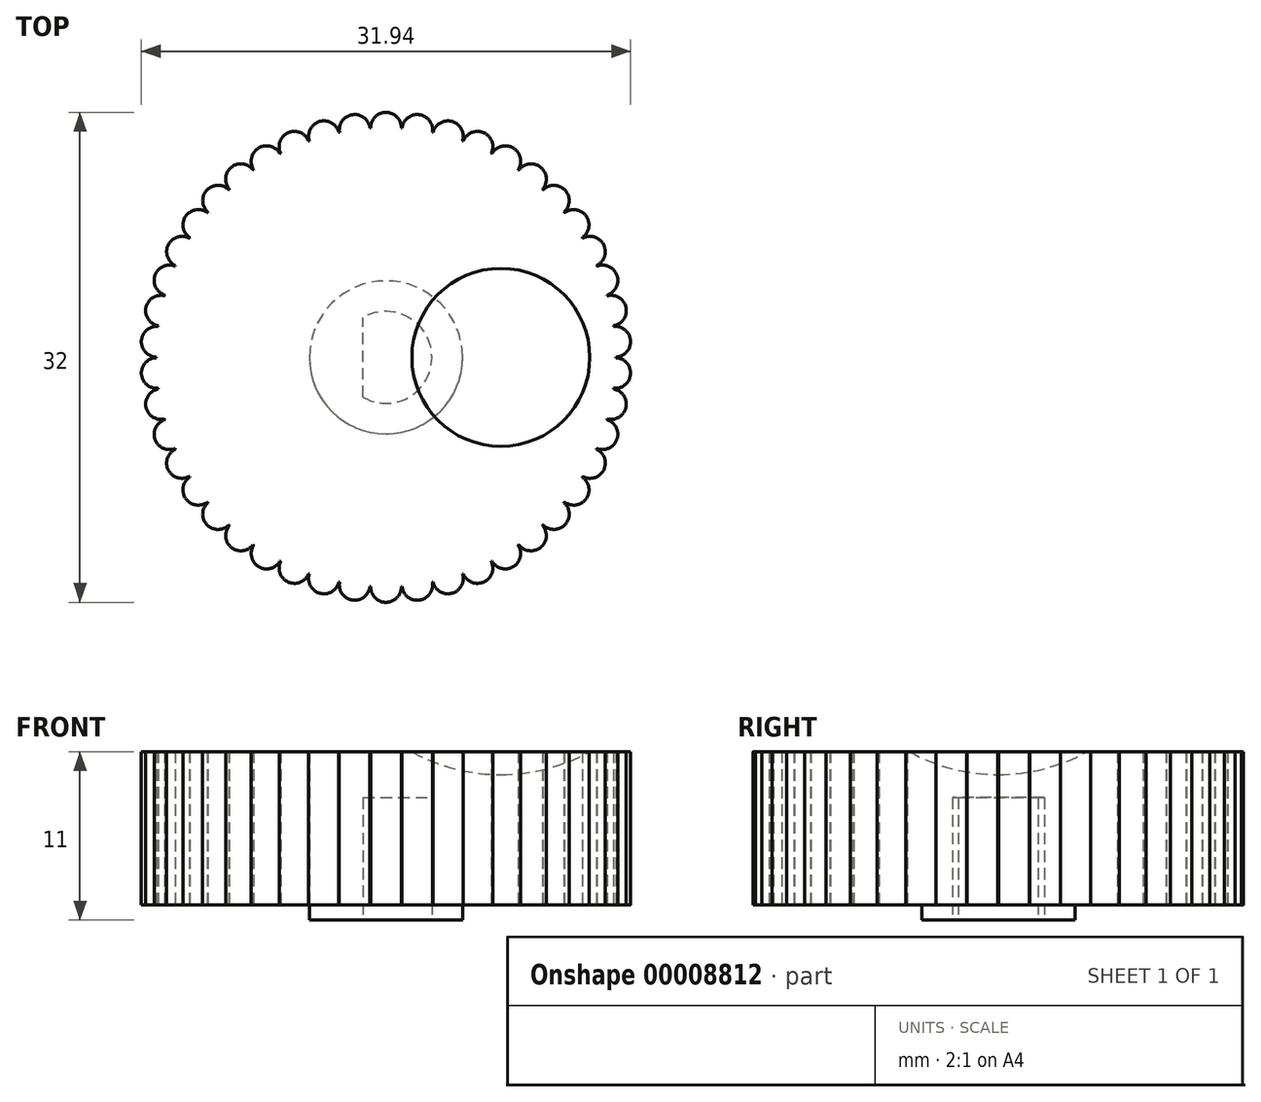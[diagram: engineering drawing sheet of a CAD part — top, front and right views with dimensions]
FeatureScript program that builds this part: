
annotation { "Feature Type Name" : "Feature", "Feature Type Description" : "" }
export const myFeature = defineFeature(function(context is Context, id is Id, definition is map)
    precondition{}
    {
        {
            var Q0;
            Q0=qCreatedBy(makeId("Top.planeOp"),FACE);
            var sketch = newSketch(context, id + "F0", { "sketchPlane" : qUnion([Q0])});
            skArc(sketch, "E0", {"start": v(1, 14.97) * mm, "mid": v(0, 16) * mm, "end": v(-1, 14.97) * mm});
            skCircle(sketch, "E1", {"center": v(0, 0) * mm, "radius": 15 * mm});
            skArc(sketch, "E2.1.0", {"start": v(-1.05, 14.96) * mm, "mid": v(-2.18, 15.85) * mm, "end": v(-3.03, 14.7) * mm});
            skArc(sketch, "E2.2.0", {"start": v(-3.08, 14.68) * mm, "mid": v(-4.32, 15.4) * mm, "end": v(-5, 14.14) * mm});
            skArc(sketch, "E2.3.0", {"start": v(-5.05, 14.13) * mm, "mid": v(-6.37, 14.68) * mm, "end": v(-6.88, 13.33) * mm});
            skArc(sketch, "E2.4.0", {"start": v(-6.92, 13.3) * mm, "mid": v(-8.31, 13.67) * mm, "end": v(-8.63, 12.27) * mm});
            skArc(sketch, "E2.5.0", {"start": v(-8.67, 12.24) * mm, "mid": v(-10.1, 12.41) * mm, "end": v(-10.22, 10.98) * mm});
            skArc(sketch, "E2.6.0", {"start": v(-10.26, 10.95) * mm, "mid": v(-11.7, 10.92) * mm, "end": v(-11.62, 9.49) * mm});
            skArc(sketch, "E2.7.0", {"start": v(-11.65, 9.45) * mm, "mid": v(-13.07, 9.23) * mm, "end": v(-12.8, 7.81) * mm});
            skArc(sketch, "E2.8.0", {"start": v(-12.83, 7.77) * mm, "mid": v(-14.2, 7.36) * mm, "end": v(-13.75, 6) * mm});
            skArc(sketch, "E2.9.0", {"start": v(-13.77, 5.95) * mm, "mid": v(-15.08, 5.36) * mm, "end": v(-14.44, 4.07) * mm});
            skArc(sketch, "E2.10.0", {"start": v(-14.45, 4.02) * mm, "mid": v(-15.67, 3.26) * mm, "end": v(-14.86, 2.07) * mm});
            skArc(sketch, "E2.11.0", {"start": v(-14.86, 2.02) * mm, "mid": v(-15.96, 1.1) * mm, "end": v(-15, 0.02) * mm});
            skArc(sketch, "E2.12.0", {"start": v(-15, -0.02) * mm, "mid": v(-15.96, -1.1) * mm, "end": v(-14.86, -2.02) * mm});
            skArc(sketch, "E2.13.0", {"start": v(-14.86, -2.07) * mm, "mid": v(-15.67, -3.26) * mm, "end": v(-14.45, -4.02) * mm});
            skArc(sketch, "E2.14.0", {"start": v(-14.44, -4.07) * mm, "mid": v(-15.08, -5.36) * mm, "end": v(-13.77, -5.95) * mm});
            skArc(sketch, "E2.15.0", {"start": v(-13.75, -6) * mm, "mid": v(-14.2, -7.36) * mm, "end": v(-12.83, -7.77) * mm});
            skArc(sketch, "E2.16.0", {"start": v(-12.8, -7.81) * mm, "mid": v(-13.07, -9.23) * mm, "end": v(-11.65, -9.45) * mm});
            skArc(sketch, "E2.17.0", {"start": v(-11.62, -9.49) * mm, "mid": v(-11.7, -10.92) * mm, "end": v(-10.26, -10.95) * mm});
            skArc(sketch, "E2.18.0", {"start": v(-10.22, -10.98) * mm, "mid": v(-10.1, -12.41) * mm, "end": v(-8.67, -12.24) * mm});
            skArc(sketch, "E2.19.0", {"start": v(-8.63, -12.27) * mm, "mid": v(-8.31, -13.67) * mm, "end": v(-6.92, -13.3) * mm});
            skArc(sketch, "E2.20.0", {"start": v(-6.88, -13.33) * mm, "mid": v(-6.37, -14.68) * mm, "end": v(-5.05, -14.13) * mm});
            skArc(sketch, "E2.21.0", {"start": v(-5, -14.14) * mm, "mid": v(-4.32, -15.4) * mm, "end": v(-3.08, -14.68) * mm});
            skArc(sketch, "E2.22.0", {"start": v(-3.03, -14.7) * mm, "mid": v(-2.18, -15.85) * mm, "end": v(-1.05, -14.96) * mm});
            skArc(sketch, "E2.23.0", {"start": v(-1, -14.97) * mm, "mid": v(0, -16) * mm, "end": v(1, -14.97) * mm});
            skArc(sketch, "E2.24.0", {"start": v(1.05, -14.96) * mm, "mid": v(2.18, -15.85) * mm, "end": v(3.03, -14.7) * mm});
            skArc(sketch, "E2.25.0", {"start": v(3.08, -14.68) * mm, "mid": v(4.32, -15.4) * mm, "end": v(5, -14.14) * mm});
            skArc(sketch, "E2.26.0", {"start": v(5.05, -14.13) * mm, "mid": v(6.37, -14.68) * mm, "end": v(6.88, -13.33) * mm});
            skArc(sketch, "E2.27.0", {"start": v(6.92, -13.3) * mm, "mid": v(8.31, -13.67) * mm, "end": v(8.63, -12.27) * mm});
            skArc(sketch, "E2.28.0", {"start": v(8.67, -12.24) * mm, "mid": v(10.1, -12.41) * mm, "end": v(10.22, -10.98) * mm});
            skArc(sketch, "E2.29.0", {"start": v(10.26, -10.95) * mm, "mid": v(11.7, -10.92) * mm, "end": v(11.62, -9.49) * mm});
            skArc(sketch, "E2.30.0", {"start": v(11.65, -9.45) * mm, "mid": v(13.07, -9.23) * mm, "end": v(12.8, -7.81) * mm});
            skArc(sketch, "E2.31.0", {"start": v(12.83, -7.77) * mm, "mid": v(14.2, -7.36) * mm, "end": v(13.75, -6) * mm});
            skArc(sketch, "E2.32.0", {"start": v(13.77, -5.95) * mm, "mid": v(15.08, -5.36) * mm, "end": v(14.44, -4.07) * mm});
            skArc(sketch, "E2.33.0", {"start": v(14.45, -4.02) * mm, "mid": v(15.67, -3.26) * mm, "end": v(14.86, -2.07) * mm});
            skArc(sketch, "E2.34.0", {"start": v(14.86, -2.02) * mm, "mid": v(15.96, -1.1) * mm, "end": v(15, -0.02) * mm});
            skArc(sketch, "E2.35.0", {"start": v(15, 0.02) * mm, "mid": v(15.96, 1.1) * mm, "end": v(14.86, 2.02) * mm});
            skArc(sketch, "E2.36.0", {"start": v(14.86, 2.07) * mm, "mid": v(15.67, 3.26) * mm, "end": v(14.45, 4.02) * mm});
            skArc(sketch, "E2.37.0", {"start": v(14.44, 4.07) * mm, "mid": v(15.08, 5.36) * mm, "end": v(13.77, 5.95) * mm});
            skArc(sketch, "E2.38.0", {"start": v(13.75, 6) * mm, "mid": v(14.2, 7.36) * mm, "end": v(12.83, 7.77) * mm});
            skArc(sketch, "E2.39.0", {"start": v(12.8, 7.81) * mm, "mid": v(13.07, 9.23) * mm, "end": v(11.65, 9.45) * mm});
            skArc(sketch, "E2.40.0", {"start": v(11.62, 9.49) * mm, "mid": v(11.7, 10.92) * mm, "end": v(10.26, 10.95) * mm});
            skArc(sketch, "E2.41.0", {"start": v(10.22, 10.98) * mm, "mid": v(10.1, 12.41) * mm, "end": v(8.67, 12.24) * mm});
            skArc(sketch, "E2.42.0", {"start": v(8.63, 12.27) * mm, "mid": v(8.31, 13.67) * mm, "end": v(6.92, 13.3) * mm});
            skArc(sketch, "E2.43.0", {"start": v(6.88, 13.33) * mm, "mid": v(6.37, 14.68) * mm, "end": v(5.05, 14.13) * mm});
            skArc(sketch, "E2.44.0", {"start": v(5, 14.14) * mm, "mid": v(4.32, 15.4) * mm, "end": v(3.08, 14.68) * mm});
            skArc(sketch, "E2.45.0", {"start": v(3.03, 14.7) * mm, "mid": v(2.18, 15.85) * mm, "end": v(1.05, 14.96) * mm});
            skSolve(sketch);
        }
        {
            var Q0;
            Q0 = qSketchRegion(id + "F0", true);
            extrude(context, id + "F1", {"entities" : qUnion([Q0]), "depth" : 10 * mm});
        }
        {
            var Q0;
            Q0=qCreatedBy(makeId("Front.planeOp"),FACE);
            var sketch = newSketch(context, id + "F2", { "sketchPlane" : qUnion([Q0])});
            skArc(sketch, "E3", {"start": v(7.5, 8.5) * mm, "mid": v(19.5, 20.5) * mm, "end": v(7.5, 32.5) * mm});
            skLineSegment(sketch, "E4", {"start": v(0, 10) * mm, "end": v(15, 10) * mm, "construction": true});
            skPoint(sketch, "E5", {"position": v(7.5, 10) * mm});
            skLineSegment(sketch, "E6", {"start": v(7.5, 32.5) * mm, "end": v(7.5, 8.5) * mm});
            skSolve(sketch);
        }
        {
            var Q0;
            Q0=makeQuery(id+"F2.imprint","IMPRINT",FACE,{"disambiguationData":[TD([[makeQuery(id+"F2.imprint","IMPRINT",EDGE,{"derivedFrom":sQuery(id+"F2.wireOp",EDGE,"E3")}),1.0]])]});
            var Q1;
            Q1=sQuery(id+"F2.wireOp",EDGE,"E6");
            revolve(context, id + "F3", {"operationType" : NewBodyOperationType.REMOVE, "entities" : qUnion([Q0]), "axis" : qUnion([Q1]), "revolveType" : RevolveType.FULL, "oppositeDirection" : true});
        }
        {
            var Q0;
            Q0=makeQuery(id+"F1.opExtrude","CAP_FACE",FACE,{"disambiguationData":[OSD([sQuery(id+"F0.wireOp",EDGE,"E0"),sQuery(id+"F0.wireOp",EDGE,"E1"),sQuery(id+"F0.wireOp",EDGE,"E2.1.0"),sQuery(id+"F0.wireOp",EDGE,"E2.2.0"),sQuery(id+"F0.wireOp",EDGE,"E2.3.0"),sQuery(id+"F0.wireOp",EDGE,"E2.4.0"),sQuery(id+"F0.wireOp",EDGE,"E2.5.0"),sQuery(id+"F0.wireOp",EDGE,"E2.6.0"),sQuery(id+"F0.wireOp",EDGE,"E2.7.0"),sQuery(id+"F0.wireOp",EDGE,"E2.8.0"),sQuery(id+"F0.wireOp",EDGE,"E2.9.0"),sQuery(id+"F0.wireOp",EDGE,"E2.10.0"),sQuery(id+"F0.wireOp",EDGE,"E2.11.0"),sQuery(id+"F0.wireOp",EDGE,"E2.12.0"),sQuery(id+"F0.wireOp",EDGE,"E2.13.0"),sQuery(id+"F0.wireOp",EDGE,"E2.14.0"),sQuery(id+"F0.wireOp",EDGE,"E2.15.0"),sQuery(id+"F0.wireOp",EDGE,"E2.16.0"),sQuery(id+"F0.wireOp",EDGE,"E2.17.0"),sQuery(id+"F0.wireOp",EDGE,"E2.18.0"),sQuery(id+"F0.wireOp",EDGE,"E2.19.0"),sQuery(id+"F0.wireOp",EDGE,"E2.20.0"),sQuery(id+"F0.wireOp",EDGE,"E2.21.0"),sQuery(id+"F0.wireOp",EDGE,"E2.22.0"),sQuery(id+"F0.wireOp",EDGE,"E2.23.0"),sQuery(id+"F0.wireOp",EDGE,"E2.24.0"),sQuery(id+"F0.wireOp",EDGE,"E2.25.0"),sQuery(id+"F0.wireOp",EDGE,"E2.26.0"),sQuery(id+"F0.wireOp",EDGE,"E2.27.0"),sQuery(id+"F0.wireOp",EDGE,"E2.28.0"),sQuery(id+"F0.wireOp",EDGE,"E2.29.0"),sQuery(id+"F0.wireOp",EDGE,"E2.30.0"),sQuery(id+"F0.wireOp",EDGE,"E2.31.0"),sQuery(id+"F0.wireOp",EDGE,"E2.32.0"),sQuery(id+"F0.wireOp",EDGE,"E2.33.0"),sQuery(id+"F0.wireOp",EDGE,"E2.34.0"),sQuery(id+"F0.wireOp",EDGE,"E2.35.0"),sQuery(id+"F0.wireOp",EDGE,"E2.36.0"),sQuery(id+"F0.wireOp",EDGE,"E2.37.0"),sQuery(id+"F0.wireOp",EDGE,"E2.38.0"),sQuery(id+"F0.wireOp",EDGE,"E2.39.0"),sQuery(id+"F0.wireOp",EDGE,"E2.40.0"),sQuery(id+"F0.wireOp",EDGE,"E2.41.0"),sQuery(id+"F0.wireOp",EDGE,"E2.42.0"),sQuery(id+"F0.wireOp",EDGE,"E2.43.0"),sQuery(id+"F0.wireOp",EDGE,"E2.44.0"),sQuery(id+"F0.wireOp",EDGE,"E2.45.0")])],"isStart":true});
            var sketch = newSketch(context, id + "F4", { "sketchPlane" : qUnion([Q0])});
            skCircle(sketch, "E7", {"center": v(0, 0) * mm, "radius": 5 * mm});
            skArc(sketch, "E8", {"start": v(-1.5, -2.6) * mm, "mid": v(3, 0) * mm, "end": v(-1.5, 2.6) * mm});
            skLineSegment(sketch, "E9", {"start": v(-1.5, 2.6) * mm, "end": v(-1.5, -2.6) * mm});
            skSolve(sketch);
        }
        {
            var Q0;
            Q0=makeQuery(id+"F4.imprint","IMPRINT",FACE,{"disambiguationData":[TD([[makeQuery(id+"F4.imprint","IMPRINT",EDGE,{"derivedFrom":sQuery(id+"F4.wireOp",EDGE,"E8")}),1.0]])]});
            extrude(context, id + "F5", {"entities" : qUnion([Q0]), "operationType" : NewBodyOperationType.REMOVE, "oppositeDirection" : true, "depth" : 7 * mm});
        }
        {
            var Q0;
            Q0 = qSketchRegion(id + "F4", true);
            extrude(context, id + "F6", {"entities" : qUnion([Q0]), "operationType" : NewBodyOperationType.ADD, "depth" : 1 * mm});
        }
    });
